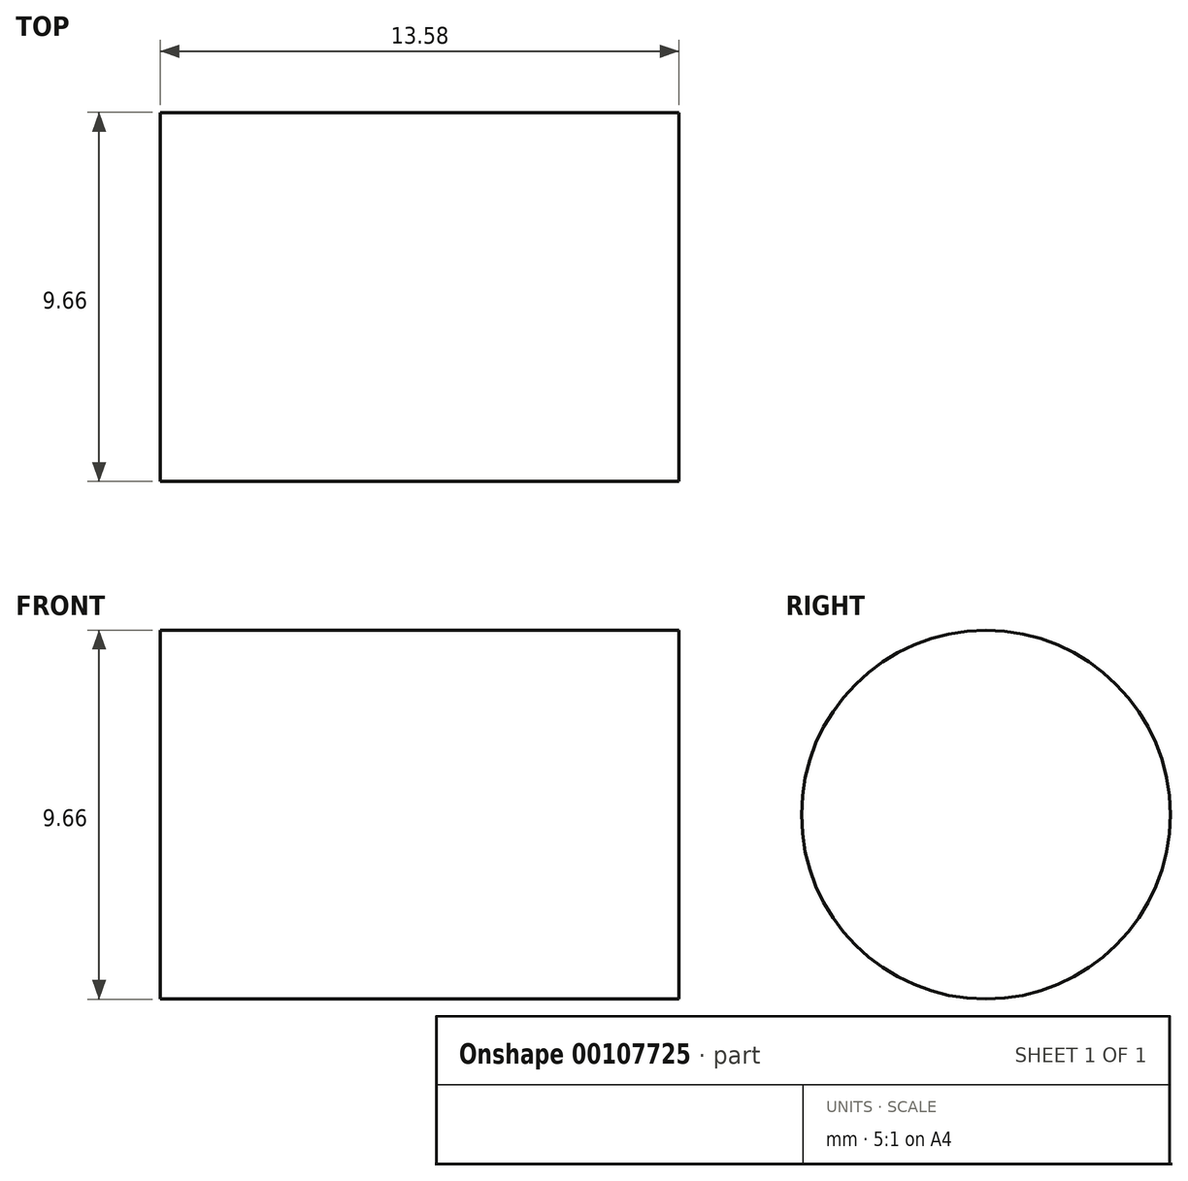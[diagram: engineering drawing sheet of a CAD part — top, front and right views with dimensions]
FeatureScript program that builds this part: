
annotation { "Feature Type Name" : "Feature", "Feature Type Description" : "" }
export const myFeature = defineFeature(function(context is Context, id is Id, definition is map)
    precondition{}
    {
        {
            var Q0;
            Q0=qCreatedBy(makeId("Right.planeOp"),FACE);
            var sketch = newSketch(context, id + "F0", { "sketchPlane" : qUnion([Q0])});
            skCircle(sketch, "E0", {"center": v(0, 0) * mm, "radius": 4.83 * mm});
            skSolve(sketch);
        }
        {
            var Q0;
            Q0=makeQuery(id+"F0.imprint","IMPRINT",FACE,{"disambiguationData":[TD([[makeQuery(id+"F0.imprint","IMPRINT",EDGE,{"derivedFrom":sQuery(id+"F0.wireOp",EDGE,"E0")}),1.0]])]});
            extrude(context, id + "F1", {"entities" : qUnion([Q0]), "endBound" : BoundingType.SYMMETRIC, "oppositeDirection" : true, "depth" : 13.58 * mm});
        }
    });
